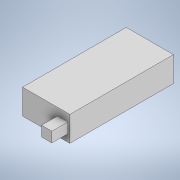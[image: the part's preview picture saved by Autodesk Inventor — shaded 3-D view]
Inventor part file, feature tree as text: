
AUTODESK INVENTOR PART (.ipt)
format: ipt  version: 2022 (Build 260153000, 153)  size: 104,448 bytes
history: native  units: mm
features: extrude x2, sketch x2
ambient origin geometry x8: Origin, YZ Plane, XZ Plane, XY Plane, X Axis, Y Axis, Z Axis, Center Point
bodies: Solid1 (feature_tree)
feature tree (4):
  extrude  "Extrusion1"  Depth=59.0mm
  extrude  "Extrusion2"  Depth=15.2mm
  sketch  "Sketch1"  dims[d0=129.5mm d1=59.0mm]
  sketch  "Sketch2"  dims[d2=31.35mm d3=0.0mm d4=15.2mm d5=12.8mm d6=12.8mm d7=20.1mm d8=0.0mm]
